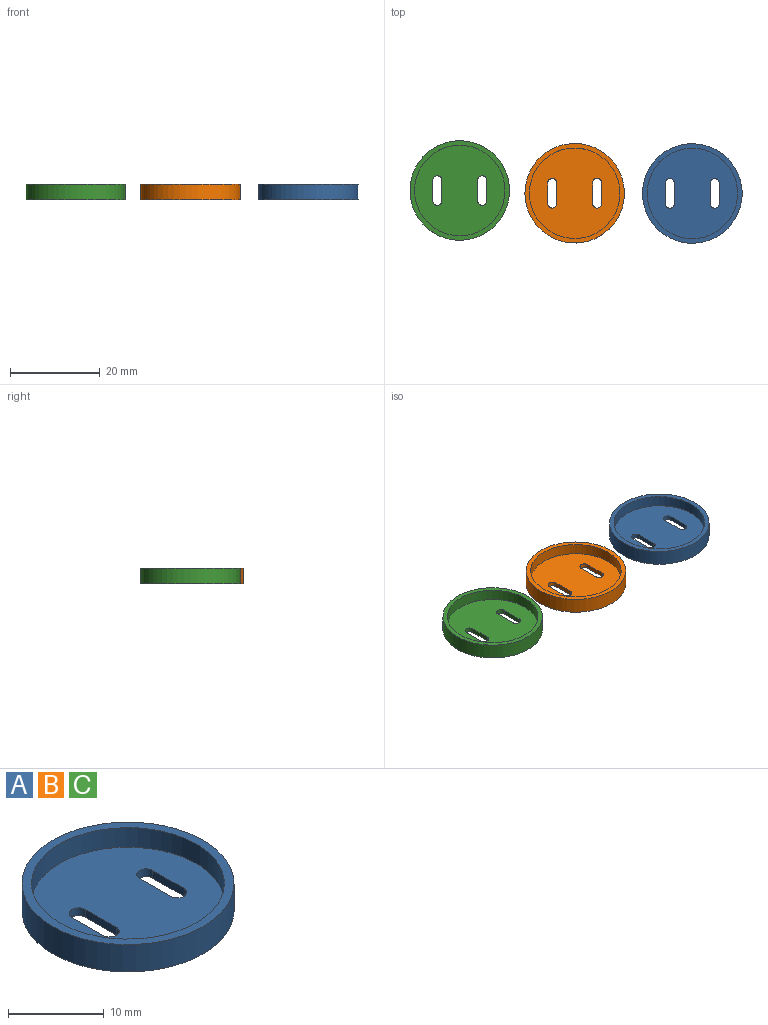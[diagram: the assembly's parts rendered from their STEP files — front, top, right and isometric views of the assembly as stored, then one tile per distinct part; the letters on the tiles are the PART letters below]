
ASSEMBLY  parts=3 mates=2
PART A: 13 faces, bbox 22.2x22.2x3.5 mm
  f0: plane 20.2x20.2mm, normal (0,0,1), area 295.8mm2, adj f4,f5,f6,f7,f8,f9,f10,f11
  f1: plane 22.2x22.2mm, normal (0,0,-1), area 362.4mm2, adj f3,f5,f6,f7,f8,f9,f10,f11
  f2: plane 22.2x22.2mm, normal (0,0,1), area 66.6mm2, adj f3,f4
  f3: cylinder r=11.1mm len=22.2mm, axis (0,0,-1), area 244.1mm2, adj f1,f2
  f4: cylinder r=10.1mm len=20.2mm, axis (0,0,-1), area 158.7mm2, adj f0,f2
  f5: cylinder r=1mm len=2mm, axis (0,0,-1), area 3.1mm2, adj f0,f1,f6,f7
  f6: plane 4.6x1mm, normal (-1,0,0), area 4.6mm2, adj f0,f1,f5,f8
  f7: plane 4.6x1mm, normal (1,0,0), area 4.6mm2, adj f0,f1,f5,f8
  f8: cylinder r=1mm len=2mm, axis (0,0,-1), area 3.1mm2, adj f0,f1,f6,f7
  f9: cylinder r=1mm len=2mm, axis (0,0,-1), area 3.1mm2, adj f0,f1,f10,f11
  f10: plane 4.6x1mm, normal (-1,0,0), area 4.6mm2, adj f0,f1,f9,f12
  f11: plane 4.6x1mm, normal (1,0,0), area 4.6mm2, adj f0,f1,f9,f12
  f12: cylinder r=1mm len=2mm, axis (0,0,-1), area 3.1mm2, adj f0,f1,f10,f11
PART B: same geometry as A
PART C: same geometry as A
PLACE A t=(51.89,-0.66,0)mm
PLACE B t=(25.63,-0.61,0)mm
PLACE C at identity fixed
MATE planar A.f3 <-> C.f3  axis (0,0,-1) through (51.89,-0.66,0)mm
MATE planar B.f3 <-> C.f3  axis (0,0,-1) through (25.63,-0.61,0)mm
